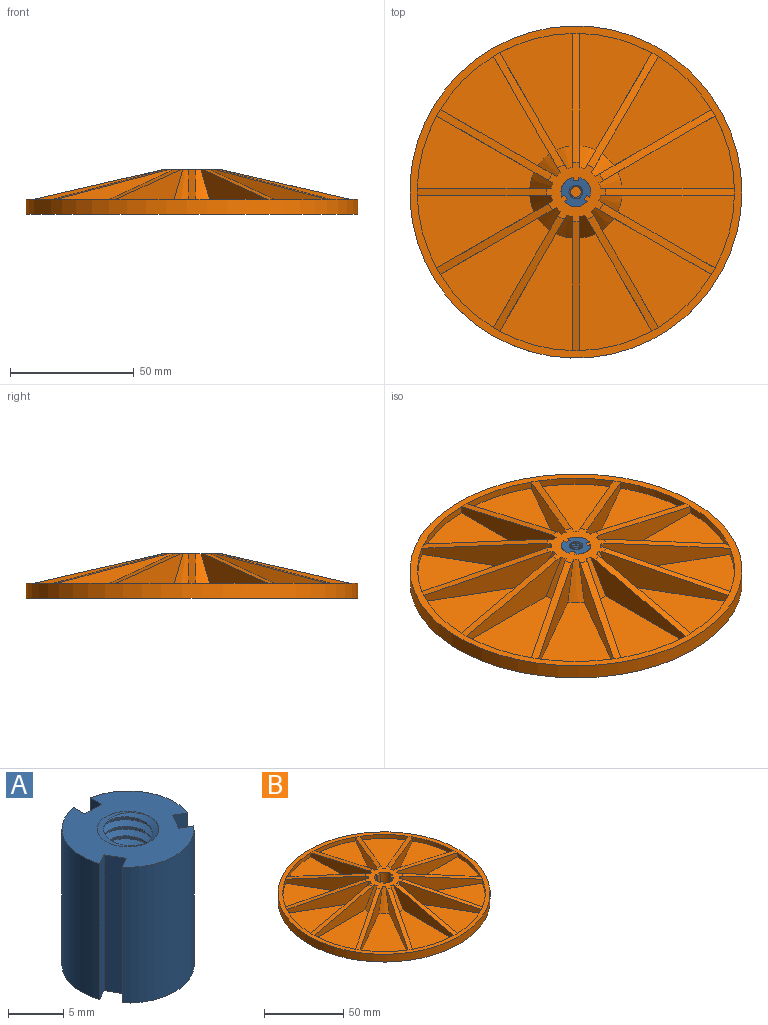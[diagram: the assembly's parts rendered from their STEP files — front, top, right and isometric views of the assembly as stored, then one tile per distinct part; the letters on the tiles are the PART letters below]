
ASSEMBLY  parts=2 mates=1
PART A: 20 faces, bbox 12.2x12.1x15.9 mm
  f0: bspline ~15.14x6.42mm, area 140.6mm2, adj f2,f3,f18,f19
  f1: bspline ~15.5x6.42mm, area 144.1mm2, adj f2,f3,f18,f19
  f2: cylinder r=2.21mm len=14.67mm, axis (0,0,-1), area 48.2mm2, adj f0,f1,f18,f19
  f3: cylinder r=2.78mm len=15mm, axis (0,0,1), area 66.3mm2, adj f0,f1,f16,f17,f18
  f4: plane 15x1.23mm, normal (-0.5,0.87,0), area 21.2mm2, adj f5,f15,f16,f17
  f5: cylinder r=5.96mm len=15mm, axis (0,0,1), area 155.6mm2, adj f4,f6,f16,f17
  f6: plane 15x1.23mm, normal (0.5,0.87,0), area 21.2mm2, adj f5,f7,f16,f17
  f7: plane 15x1.82mm, normal (0.87,-0.5,0), area 31.5mm2, adj f6,f8,f16,f17
  f8: plane 15x1.23mm, normal (-0.5,-0.87,0), area 21.2mm2, adj f7,f9,f16,f17
  f9: cylinder r=5.96mm len=15mm, axis (0,0,1), area 155.6mm2, adj f8,f10,f16,f17
  f10: plane 15x1.42mm, normal (-1,0,0), area 21.2mm2, adj f9,f11,f16,f17
  f11: plane 15x2.1mm, normal (0,1,0), area 31.5mm2, adj f10,f12,f16,f17
  f12: plane 15x1.42mm, normal (1,0,0), area 21.2mm2, adj f11,f13,f16,f17
  f13: cylinder r=5.96mm len=15mm, axis (0,0,1), area 155.6mm2, adj f12,f14,f16,f17
  f14: plane 15x1.23mm, normal (0.5,-0.87,0), area 21.2mm2, adj f13,f15,f16,f17
  f15: plane 15x1.82mm, normal (-0.87,-0.5,0), area 31.5mm2, adj f4,f14,f16,f17
  f16: plane 11.92x11.83mm, normal (0,0,-1), area 78mm2, adj f3,f4,f5,f6,f7,f8,f9,f10
  f17: plane 11.92x11.83mm, normal (0,0,1), area 78mm2, adj f3,f4,f5,f6,f7,f8,f9,f10
  f18: plane 0.79x0.52mm, normal (-0.44,0.9,0), area 0.3mm2, adj f0,f1,f2,f3
  f19: plane 5.85x5.85mm, normal (0,0,1), area 4mm2, adj f0,f1,f2,f17
PART B: 89 faces, bbox 134.3x134.3x18.3 mm
  f0: plane 24x24mm, normal (0,0,1), area 282.1mm2, adj f23,f24,f25,f26,f27,f28,f29,f30
  f1: cylinder r=64mm len=29.19mm, axis (0,0,-1), area 91.5mm2, adj f14,f35,f68,f74
  f2: cylinder r=64mm len=29.19mm, axis (0,0,-1), area 91.5mm2, adj f13,f35,f50,f70
  f3: cylinder r=64mm len=21.37mm, axis (0,0,-1), area 91.5mm2, adj f18,f35,f56,f67
  f4: cylinder r=64mm len=29.19mm, axis (0,0,-1), area 91.5mm2, adj f16,f35,f62,f64
  f5: cylinder r=64mm len=21.37mm, axis (0,0,-1), area 91.5mm2, adj f17,f35,f59,f61
  f6: cylinder r=64mm len=29.19mm, axis (0,0,-1), area 91.5mm2, adj f19,f35,f58,f71
  f7: cylinder r=64mm len=29.19mm, axis (0,0,-1), area 91.5mm2, adj f15,f35,f55,f65
  f8: cylinder r=64mm len=29.19mm, axis (0,0,-1), area 91.5mm2, adj f20,f35,f47,f52
  f9: cylinder r=64mm len=21.37mm, axis (0,0,-1), area 91.5mm2, adj f21,f35,f49,f53
  f10: cylinder r=64mm len=29.19mm, axis (0,0,-1), area 91.5mm2, adj f22,f35,f41,f46
  f11: cylinder r=64mm len=29.19mm, axis (0,0,-1), area 91.5mm2, adj f12,f35,f43,f73
  f12: plane 47.12x29.19mm, normal (0,0,1), area 845.1mm2, adj f11,f23,f43,f73
  f13: plane 47.12x29.19mm, normal (0,0,1), area 845.1mm2, adj f2,f24,f50,f70
  f14: plane 47.12x29.19mm, normal (0,0,1), area 845.1mm2, adj f1,f25,f68,f74
  f15: plane 47.12x29.19mm, normal (0,0,1), area 845.1mm2, adj f7,f26,f55,f65
  f16: plane 47.12x29.19mm, normal (0,0,1), area 845.1mm2, adj f4,f27,f62,f64
  f17: plane 44.06x44.06mm, normal (0,0,1), area 845.1mm2, adj f5,f28,f59,f61
  f18: plane 44.06x44.06mm, normal (0,0,1), area 845.1mm2, adj f3,f29,f56,f67
  f19: plane 47.12x29.19mm, normal (0,0,1), area 845.1mm2, adj f6,f30,f58,f71
  f20: plane 47.12x29.19mm, normal (0,0,1), area 845.1mm2, adj f8,f31,f47,f52
  f21: plane 44.06x44.06mm, normal (0,0,1), area 845.1mm2, adj f9,f32,f49,f53
  f22: plane 47.12x29.19mm, normal (0,0,1), area 845.1mm2, adj f10,f33,f41,f46
  f23: cone r=10mm half-angle=30deg, axis (0,0,-1), area 74.4mm2, adj f0,f12,f43,f73
  f24: cone r=10mm half-angle=30deg, axis (0,0,-1), area 74.4mm2, adj f0,f13,f50,f70
  f25: cone r=10mm half-angle=30deg, axis (0,0,-1), area 74.4mm2, adj f0,f14,f68,f74
  f26: cone r=10mm half-angle=30deg, axis (0,0,-1), area 74.4mm2, adj f0,f15,f55,f65
  f27: cone r=10mm half-angle=30deg, axis (0,0,-1), area 74.4mm2, adj f0,f16,f62,f64
  f28: cone r=10mm half-angle=30deg, axis (0,0,-1), area 74.4mm2, adj f0,f17,f59,f61
  f29: cone r=10mm half-angle=30deg, axis (0,0,-1), area 74.4mm2, adj f0,f18,f56,f67
  f30: cone r=10mm half-angle=30deg, axis (0,0,-1), area 74.4mm2, adj f0,f19,f58,f71
  f31: cone r=10mm half-angle=30deg, axis (0,0,-1), area 74.4mm2, adj f0,f20,f47,f52
  f32: cone r=10mm half-angle=30deg, axis (0,0,-1), area 74.4mm2, adj f0,f21,f49,f53
  f33: cone r=10mm half-angle=30deg, axis (0,0,-1), area 74.4mm2, adj f0,f22,f41,f46
  f34: cylinder r=67mm len=134mm, axis (0,0,-1), area 2525.8mm2, adj f35,f36
  f35: plane 134x134mm, normal (0,0,1), area 1234.6mm2, adj f1,f2,f3,f4,f5,f6,f7,f8
  f36: plane 134x134mm, normal (0,0,-1), area 14102.6mm2, adj f34
  f37: cylinder r=64mm len=21.37mm, axis (0,0,-1), area 91.5mm2, adj f35,f38,f40,f44
  f38: plane 44.06x44.06mm, normal (0,0,1), area 845.1mm2, adj f37,f39,f40,f44
  f39: cone r=10mm half-angle=30deg, axis (0,0,-1), area 74.4mm2, adj f0,f38,f40,f44
  f40: plane 47.15x27.35mm, normal (0.87,0.5,0), area 433.8mm2, adj f0,f37,f38,f39,f42
  f41: plane 47.15x27.35mm, normal (-0.87,-0.5,0), area 433.8mm2, adj f0,f10,f22,f33,f42
  f42: cone r=64mm half-angle=77deg, axis (0,0,-1), area 160.2mm2, adj f0,f35,f40,f41
  f43: plane 47.15x27.35mm, normal (0.5,0.87,0), area 433.8mm2, adj f0,f11,f12,f23,f45
  f44: plane 47.15x27.35mm, normal (-0.5,-0.87,0), area 433.8mm2, adj f0,f37,f38,f39,f45
  f45: cone r=64mm half-angle=77deg, axis (0,0,-1), area 160.2mm2, adj f0,f35,f43,f44
  f46: plane 54.4x15.31mm, normal (1,0,0), area 433.8mm2, adj f0,f10,f22,f33,f48
  f47: plane 54.4x15.31mm, normal (-1,0,0), area 433.8mm2, adj f0,f8,f20,f31,f48
  f48: cone r=64mm half-angle=77deg, axis (0,0,-1), area 160.2mm2, adj f0,f35,f46,f47
  f49: plane 47.15x27.35mm, normal (0.5,-0.87,0), area 433.8mm2, adj f0,f9,f21,f32,f51
  f50: plane 47.15x27.35mm, normal (-0.5,0.87,0), area 433.8mm2, adj f0,f2,f13,f24,f51
  f51: cone r=64mm half-angle=77deg, axis (0,0,-1), area 160.2mm2, adj f0,f35,f49,f50
  f52: plane 47.15x27.35mm, normal (0.87,-0.5,0), area 433.8mm2, adj f0,f8,f20,f31,f54
  f53: plane 47.15x27.35mm, normal (-0.87,0.5,0), area 433.8mm2, adj f0,f9,f21,f32,f54
  f54: cone r=64mm half-angle=77deg, axis (0,0,-1), area 160.2mm2, adj f0,f35,f52,f53
  f55: plane 47.15x27.35mm, normal (-0.87,0.5,0), area 433.8mm2, adj f0,f7,f15,f26,f57
  f56: plane 47.15x27.35mm, normal (0.87,-0.5,0), area 433.8mm2, adj f0,f3,f18,f29,f57
  f57: cone r=64mm half-angle=77deg, axis (0,0,-1), area 160.2mm2, adj f0,f35,f55,f56
  f58: plane 47.15x27.35mm, normal (-0.5,-0.87,0), area 433.8mm2, adj f0,f6,f19,f30,f60
  f59: plane 47.15x27.35mm, normal (0.5,0.87,0), area 433.8mm2, adj f0,f5,f17,f28,f60
  f60: cone r=64mm half-angle=77deg, axis (0,0,-1), area 160.2mm2, adj f0,f35,f58,f59
  f61: plane 47.15x27.35mm, normal (-0.87,-0.5,0), area 433.8mm2, adj f0,f5,f17,f28,f63
  f62: plane 47.15x27.35mm, normal (0.87,0.5,0), area 433.8mm2, adj f0,f4,f16,f27,f63
  f63: cone r=64mm half-angle=77deg, axis (0,0,-1), area 160.2mm2, adj f0,f35,f61,f62
  f64: plane 54.4x15.31mm, normal (-1,0,0), area 433.8mm2, adj f0,f4,f16,f27,f66
  f65: plane 54.4x15.31mm, normal (1,0,0), area 433.8mm2, adj f0,f7,f15,f26,f66
  f66: cone r=64mm half-angle=77deg, axis (0,0,-1), area 160.2mm2, adj f0,f35,f64,f65
  f67: plane 47.15x27.35mm, normal (-0.5,0.87,0), area 433.8mm2, adj f0,f3,f18,f29,f69
  f68: plane 47.15x27.35mm, normal (0.5,-0.87,0), area 433.8mm2, adj f0,f1,f14,f25,f69
  f69: cone r=64mm half-angle=77deg, axis (0,0,-1), area 160.2mm2, adj f0,f35,f67,f68
  f70: plane 54.4x15.31mm, normal (0,-1,0), area 433.8mm2, adj f0,f2,f13,f24,f72
  f71: plane 54.4x15.31mm, normal (0,1,0), area 433.8mm2, adj f0,f6,f19,f30,f72
  f72: cone r=64mm half-angle=77deg, axis (0,0,-1), area 160.2mm2, adj f0,f35,f70,f71
  f73: plane 54.4x15.31mm, normal (0,-1,0), area 433.8mm2, adj f0,f11,f12,f23,f75
  f74: plane 54.4x15.31mm, normal (0,1,0), area 433.8mm2, adj f0,f1,f14,f25,f75
  f75: cone r=64mm half-angle=77deg, axis (0,0,-1), area 160.2mm2, adj f0,f35,f73,f74
  f76: plane 12x11.92mm, normal (0,0,1), area 104.3mm2, adj f77,f78,f79,f80,f81,f82,f83,f84
  f77: plane 15x1.23mm, normal (-0.5,0.87,0), area 21.2mm2, adj f0,f76,f78,f88
  f78: plane 15x1.73mm, normal (0.87,0.5,0), area 30mm2, adj f0,f76,f77,f79
  f79: plane 15x1.23mm, normal (0.5,-0.87,0), area 21.2mm2, adj f0,f76,f78,f80
  f80: cylinder r=6mm len=15mm, axis (0,0,1), area 158.4mm2, adj f0,f76,f79,f81
  f81: plane 15x1.23mm, normal (-0.5,-0.87,0), area 21.2mm2, adj f0,f76,f80,f82
  f82: plane 15x1.73mm, normal (-0.87,0.5,0), area 30mm2, adj f0,f76,f81,f83
  f83: plane 15x1.23mm, normal (0.5,0.87,0), area 21.2mm2, adj f0,f76,f82,f84
  f84: cylinder r=6mm len=15mm, axis (0,0,1), area 158.4mm2, adj f0,f76,f83,f85
  f85: plane 15x1.42mm, normal (1,0,0), area 21.2mm2, adj f0,f76,f84,f86
  f86: plane 15x2mm, normal (0,-1,0), area 30mm2, adj f0,f76,f85,f87
  f87: plane 15x1.42mm, normal (-1,0,0), area 21.2mm2, adj f0,f76,f86,f88
  f88: cylinder r=6mm len=15mm, axis (0,0,1), area 158.4mm2, adj f0,f76,f77,f87
PLACE A at identity
PLACE B at identity fixed
MATE fastened B.f1 <-> A.f2  axis (0,0,1) through (0,0,3)mm
